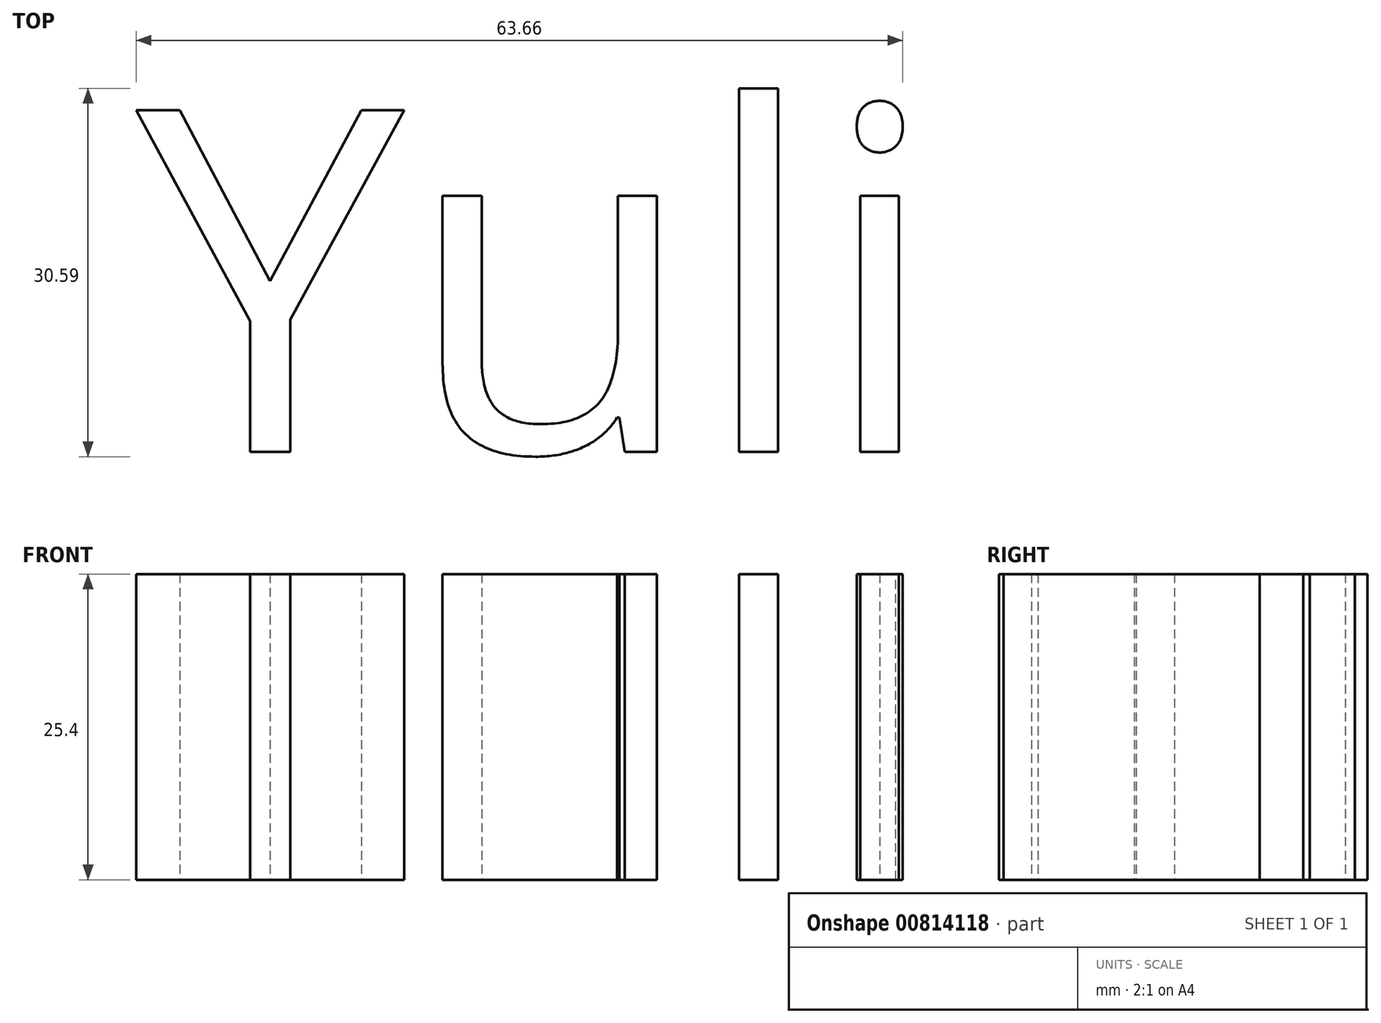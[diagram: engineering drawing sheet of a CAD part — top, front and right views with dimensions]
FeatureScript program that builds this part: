
annotation { "Feature Type Name" : "Feature", "Feature Type Description" : "" }
export const myFeature = defineFeature(function(context is Context, id is Id, definition is map)
    precondition{}
    {
        {
            var Q0;
            Q0=qCreatedBy(makeId("Top.planeOp"),FACE);
            var sketch = newSketch(context, id + "F0", { "sketchPlane" : qUnion([Q0])});
            skText(sketch, "E0", { "text": "Yuli", "fontName": "OpenSans-Regular.ttf"});
            const initialGuessF0  = {"E0": [-0.01645, 0.00613, 1, 0, 0.02862]};
            skSetInitialGuess(sketch, initialGuessF0);
            skSolve(sketch);
        }
        {
            var Q0;
            Q0 = qSketchRegion(id + "F0", true);
            extrude(context, id + "F1", {"entities" : qUnion([Q0]), "depth" : 25.4 * mm, "offsetDistance" : 25.4 * mm});
        }
    });
